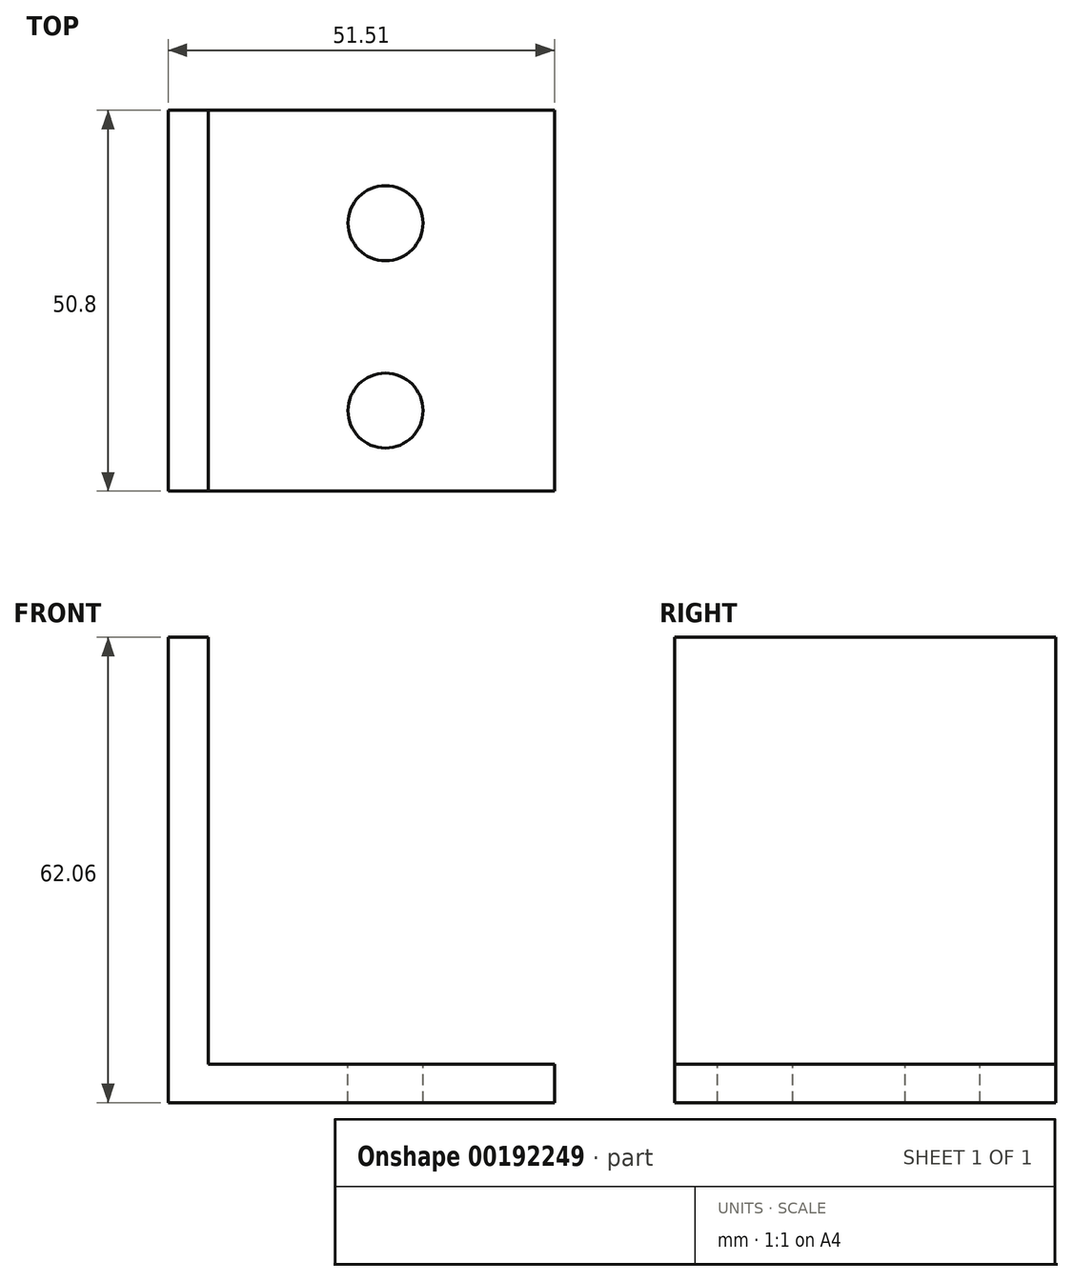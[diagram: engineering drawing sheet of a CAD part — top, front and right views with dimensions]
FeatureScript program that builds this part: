
annotation { "Feature Type Name" : "Feature", "Feature Type Description" : "" }
export const myFeature = defineFeature(function(context is Context, id is Id, definition is map)
    precondition{}
    {
        {
            var Q0;
            Q0=qCreatedBy(makeId("Front.planeOp"),FACE);
            var sketch = newSketch(context, id + "F0", { "sketchPlane" : qUnion([Q0])});
            skLineSegment(sketch, "E0", {"start": v(0, 0) * mm, "end": v(-51.5, 0) * mm});
            skLineSegment(sketch, "E1", {"start": v(-51.5, 0) * mm, "end": v(-51.5, 62.06) * mm});
            skLineSegment(sketch, "E2", {"start": v(-51.5, 62.06) * mm, "end": v(-46.14, 62.06) * mm});
            skLineSegment(sketch, "E3", {"start": v(-46.14, 62.06) * mm, "end": v(-46.14, 5.1) * mm});
            skLineSegment(sketch, "E4", {"start": v(-46.14, 5.1) * mm, "end": v(0, 5.1) * mm});
            skLineSegment(sketch, "E5", {"start": v(0, 5.1) * mm, "end": v(0, 0) * mm});
            skSolve(sketch);
        }
        {
            var Q0;
            Q0=makeQuery(id+"F0.imprint","IMPRINT",FACE,{"disambiguationData":[TD([[makeQuery(id+"F0.imprint","IMPRINT",EDGE,{"derivedFrom":sQuery(id+"F0.wireOp",EDGE,"E0")}),-1.0]])]});
            extrude(context, id + "F1", {"entities" : qUnion([Q0]), "depth" : 50.8 * mm});
        }
        {
            var Q0;
            Q0=makeQuery(id+"F1.opExtrude","SWEPT_FACE",FACE,{"disambiguationData":[OSD([sQuery(id+"F0.wireOp",EDGE,"E4")])]});
            var sketch = newSketch(context, id + "F2", { "sketchPlane" : qUnion([Q0])});
            skCircle(sketch, "E6", {"center": v(-22.53, -40.07) * mm, "radius": 5 * mm});
            skCircle(sketch, "E7", {"center": v(-22.53, -15.07) * mm, "radius": 5 * mm});
            skSolve(sketch);
        }
        {
            var Q0;
            Q0 = qSketchRegion(id + "F2", true);
            extrude(context, id + "F3", {"entities" : qUnion([Q0]), "operationType" : NewBodyOperationType.REMOVE, "oppositeDirection" : true, "depth" : 25 * mm});
        }
    });
